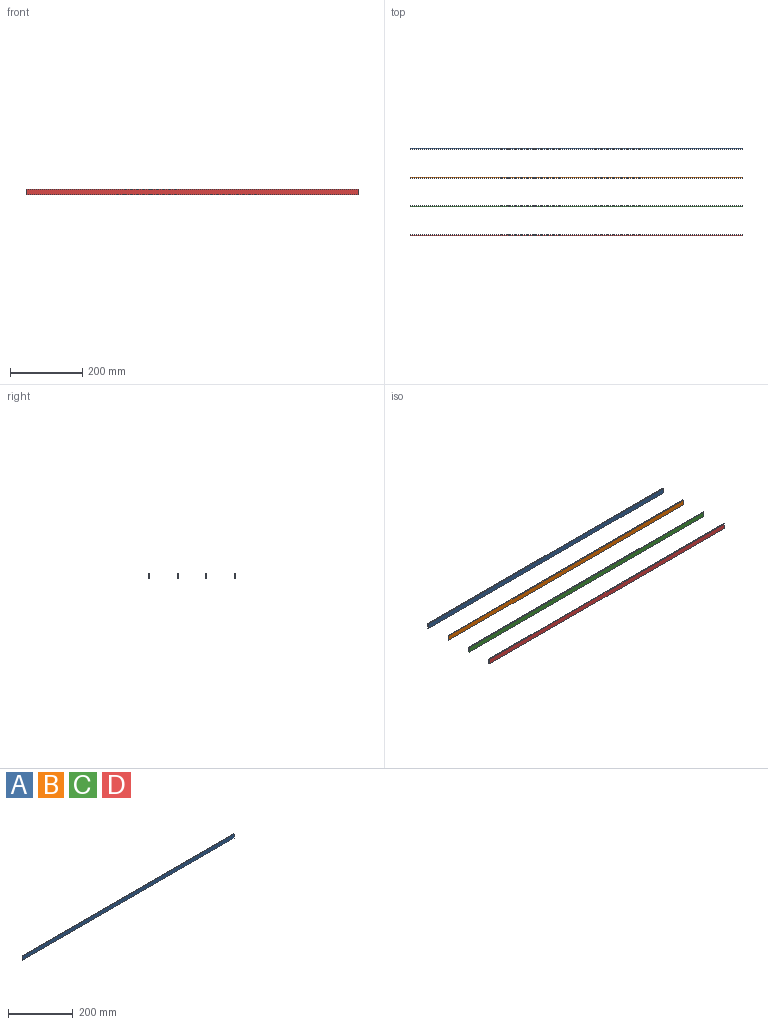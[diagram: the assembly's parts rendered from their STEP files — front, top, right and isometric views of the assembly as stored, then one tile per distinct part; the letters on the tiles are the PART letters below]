
ASSEMBLY  parts=4 mates=3
PART A: 6 faces, bbox 920x3x15 mm
  f0: plane 920x3mm, normal (0,0,-1), area 2760mm2, adj f1,f3,f4,f5
  f1: plane 15x3mm, normal (1,0,0), area 45mm2, adj f0,f2,f4,f5
  f2: plane 920x3mm, normal (0,0,1), area 2760mm2, adj f1,f3,f4,f5
  f3: plane 15x3mm, normal (-1,0,0), area 45mm2, adj f0,f2,f4,f5
  f4: plane 920x15mm, normal (0,-1,0), area 13800mm2, adj f0,f1,f2,f3
  f5: plane 920x15mm, normal (0,1,0), area 13800mm2, adj f0,f1,f2,f3
PART B: same geometry as A
PART C: same geometry as A
PART D: same geometry as A
PLACE A t=(0,226.81,0)mm
PLACE B t=(0,146.81,0)mm
PLACE C t=(0,66.81,0)mm
PLACE D t=(0,-13.19,0)mm
MATE fastened D.f2 <-> C.f2  axis (0,0,1) through (460,-16.19,7.5)mm
MATE fastened A.f2 <-> B.f2  axis (0,0,1) through (460,223.81,7.5)mm
MATE fastened C.f2 <-> B.f2  axis (0,0,1) through (460,63.81,7.5)mm
